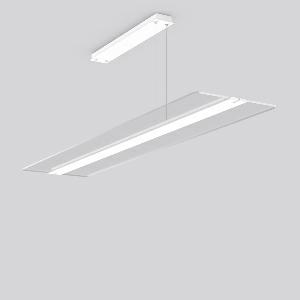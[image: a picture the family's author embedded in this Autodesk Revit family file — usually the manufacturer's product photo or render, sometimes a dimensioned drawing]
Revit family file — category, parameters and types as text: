
# Revit family: twindot_s_312265_002_76_d193
name_source: partatom
category: Lighting Fixtures
units: mm (PartAtom-declared; Revit-internal decimal feet)

## family parameters
Cut with Voids When Loaded = No
Host = Face
Light Source = No
Part Type = Normal
Room Calculation Point = No
Round Connector Dimension = Use Diameter
Shared = No

## types (1)
- TWINDOT S (1 x LED Modul 830, 8100 lm, 3000)
    Apparent Load = 65 VA
    CIE Flux Codes = 47 77 94 55 100
    Color Rendering = 80
    Color Temperature = 3000
    Default Elevation = 1800 mm
    Description = Series: TWINDOT S
LED pendant luminaire with extremely flat and frameless appearance. Middle bar made of aluminium extrusion profile, powder-coated. Transparent light guide made of UV-resistant acrylic glass (PMMA) with TWINDOT prismatic. Light control with perfectly glare-free TWINDOT technology for pleasantly gentle light with soft shadows. Even and wide indirect and direct light distribution. Direct 55%, indirect 45% light emission. 4-point steel cable suspension, steplessly adjustable. Converter integrated in the canopy (powder-coated white). Power supply through suspension cable. 
Colour: traffic white, matt (RAL 9016)
Length: 1500 mm
Width: 350 mm
Height: 20 mm
Suspension length: 500-1200 mm
Lamp: LED
Socket: without socket
Colour temperature: 3000K
Colour rendering index (CRI): 80
System power: 65 W
Rated luminous flux: 8100 lm
Luminous efficiency: 125 lm/W
Control gear: Converter, dimmable, DALI
Protection class: I
Type of protection: IP 20
    Height = 20 mm  [stored 0.0656168 ft]
    Lamp = 1 x LED Modul 830
    Lamp Light Flux = 8100 lm
    Lamp count = 1
    Length = 1500 mm
    Lifetime = 50000 h
    Luminous efficacy = 125 lm/W
    Manufacturer = RZB
    ModVariant = No
    Model = 312265.002.76
    Mounting Place = Ceiling
    Mounting Type = Pendant
    Number of Poles = 1
    OnlyDefault = Yes
    Power Factor = 1
    Product Name = TWINDOT S
    Product group = Pendant modular luminaires
    ProductGroupID = 906
    Protection Class = Protection class I
    Protection Degree = IP 20
    RLX_Detail_Level = 1
    RLX_Emergency_Light_Flux = 0 lm
    RLX_Emergency_Type = 0
    RLX_Emergency_Type_DB = No
    RlxData = <blob elided: 36673 chars, md5=2536552e>
    Socket = socket
    Standby Power = 0 W
    System Light Flux = 8100 lm
    System Power = 65 W
    Type Comments = Product without accessories
    Type Image = 312265.002.jpg
    URL = http://relux.com
    VarID = ---
    Voltage = 230 V
    Voltage Range = 220-240 V
    Weight = 0.00 kg
    Width = 350 mm

note: [stored X ft] marks values corroborated as IEEE doubles in the binary element streams (Revit-internal decimal feet)

## geometry (parser evidence)
native form markers: Blend x4, Sweep x11
no freeform markers — native parametric forms only
